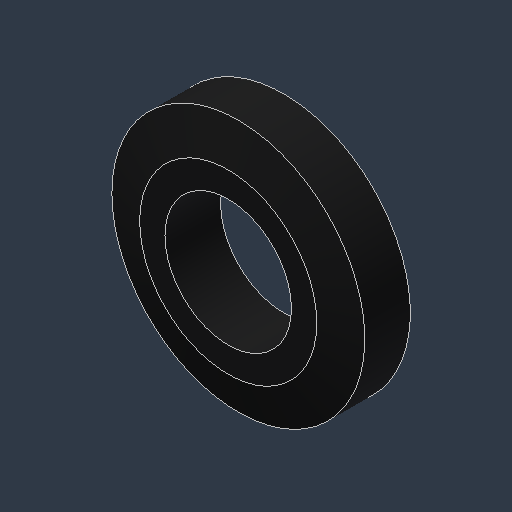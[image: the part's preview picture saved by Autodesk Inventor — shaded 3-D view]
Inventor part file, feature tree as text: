
AUTODESK INVENTOR PART (.ipt)
format: ipt  version: 2024.3 (Build 283343000, 343)  size: 100,864 bytes
history: native  units: mm (DEFAULTED — no unit token found)
features: revolve x1, sketch x1
ambient origin geometry x8: Origin, YZ Plane, XZ Plane, XY Plane, X Axis, Y Axis, Z Axis, Center Point
bodies: Solid1 (feature_tree)
feature tree (2):
  revolve  "Revolution1"  [1 undecoded]
  sketch  "Sketch2"  dims[d0=6.35mm d1=12.7mm d3=90.0deg d7=2.794mm d8=15.0deg d9=1.27mm]
note: 1 required parameter value undecoded (feature->parameter linkage not recoverable at this tier; creation-order binding heuristic only, values carry confidence <= 0.55)
